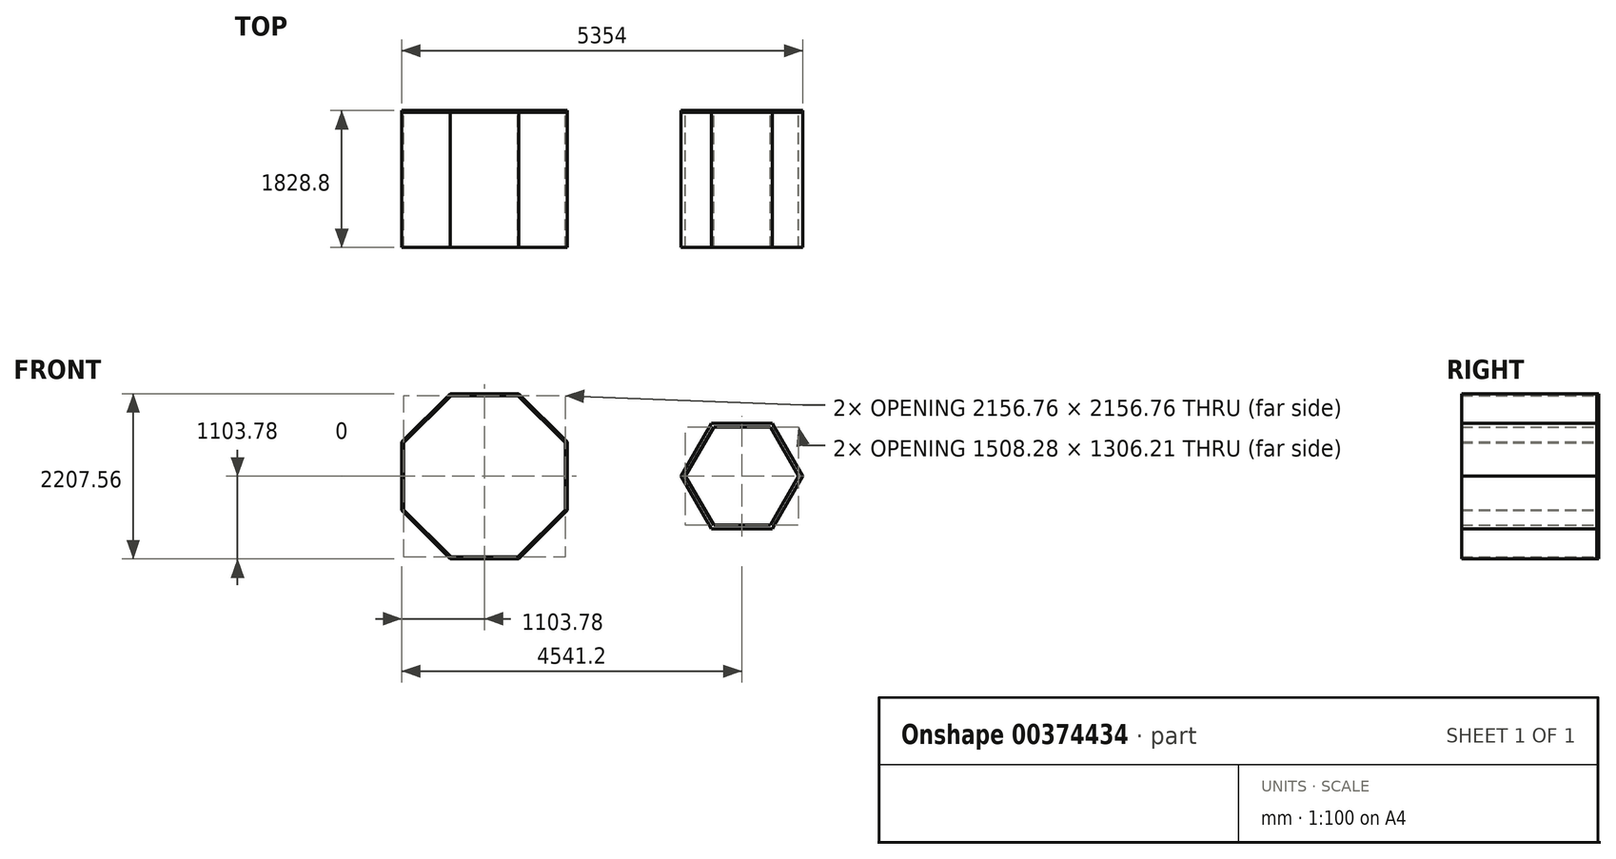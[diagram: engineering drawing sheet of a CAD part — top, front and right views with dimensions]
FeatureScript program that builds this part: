
annotation { "Feature Type Name" : "Feature", "Feature Type Description" : "" }
export const myFeature = defineFeature(function(context is Context, id is Id, definition is map)
    precondition{}
    {
        {
            var Q0;
            Q0=qCreatedBy(makeId("Front.planeOp"),FACE);
            var sketch = newSketch(context, id + "F0", { "sketchPlane" : qUnion([Q0])});
            skCircle(sketch, "E0.cCircle", {"center": v(0, 0) * mm, "radius": 812.8 * mm, "construction": true});
            skLineSegment(sketch, "E0.0", {"start": v(812.8, 0) * mm, "end": v(406.4, -703.9) * mm});
            skLineSegment(sketch, "E0.1", {"start": v(406.4, -703.9) * mm, "end": v(-406.4, -703.9) * mm});
            skLineSegment(sketch, "E0.2", {"start": v(-406.4, -703.9) * mm, "end": v(-812.8, 0) * mm});
            skLineSegment(sketch, "E0.3", {"start": v(-812.8, 0) * mm, "end": v(-406.4, 703.9) * mm});
            skLineSegment(sketch, "E0.4", {"start": v(-406.4, 703.9) * mm, "end": v(406.4, 703.9) * mm});
            skLineSegment(sketch, "E0.5", {"start": v(406.4, 703.9) * mm, "end": v(812.8, 0) * mm});
            skLineSegment(sketch, "E1.0", {"start": v(-754.14, 0) * mm, "end": v(-377.07, 653.1) * mm});
            skLineSegment(sketch, "E1.1", {"start": v(377.07, 653.1) * mm, "end": v(754.14, 0) * mm});
            skLineSegment(sketch, "E1.2", {"start": v(754.14, 0) * mm, "end": v(377.07, -653.1) * mm});
            skLineSegment(sketch, "E1.3", {"start": v(-377.07, 653.1) * mm, "end": v(377.07, 653.1) * mm});
            skLineSegment(sketch, "E1.4", {"start": v(377.07, -653.1) * mm, "end": v(-377.07, -653.1) * mm});
            skLineSegment(sketch, "E1.5", {"start": v(-377.07, -653.1) * mm, "end": v(-754.14, 0) * mm});
            skCircle(sketch, "E2.cCircle", {"center": v(-3437.42, 0) * mm, "radius": 1103.78 * mm, "construction": true});
            skLineSegment(sketch, "E2.0", {"start": v(-2980.22, -1103.78) * mm, "end": v(-3894.62, -1103.78) * mm});
            skLineSegment(sketch, "E2.1", {"start": v(-3894.62, -1103.78) * mm, "end": v(-4541.2, -457.2) * mm});
            skLineSegment(sketch, "E2.2", {"start": v(-4541.2, -457.2) * mm, "end": v(-4541.2, 457.2) * mm});
            skLineSegment(sketch, "E2.3", {"start": v(-4541.2, 457.2) * mm, "end": v(-3894.62, 1103.78) * mm});
            skLineSegment(sketch, "E2.4", {"start": v(-3894.62, 1103.78) * mm, "end": v(-2980.22, 1103.78) * mm});
            skLineSegment(sketch, "E2.5", {"start": v(-2980.22, 1103.78) * mm, "end": v(-2333.64, 457.2) * mm});
            skLineSegment(sketch, "E2.6", {"start": v(-2333.64, 457.2) * mm, "end": v(-2333.64, -457.2) * mm});
            skLineSegment(sketch, "E2.7", {"start": v(-2333.64, -457.2) * mm, "end": v(-2980.22, -1103.78) * mm});
            skPoint(sketch, "E2.0.midPoint", {"position": v(-3437.42, -1103.78) * mm});
            skLineSegment(sketch, "E3.0", {"start": v(-4515.8, 446.68) * mm, "end": v(-3884.1, 1078.38) * mm});
            skLineSegment(sketch, "E3.1", {"start": v(-4515.8, -446.68) * mm, "end": v(-4515.8, 446.68) * mm});
            skLineSegment(sketch, "E3.2", {"start": v(-3884.1, 1078.38) * mm, "end": v(-2990.74, 1078.38) * mm});
            skLineSegment(sketch, "E3.3", {"start": v(-3884.1, -1078.38) * mm, "end": v(-4515.8, -446.68) * mm});
            skLineSegment(sketch, "E3.4", {"start": v(-2990.74, 1078.38) * mm, "end": v(-2359.04, 446.68) * mm});
            skLineSegment(sketch, "E3.5", {"start": v(-2359.04, 446.68) * mm, "end": v(-2359.04, -446.68) * mm});
            skLineSegment(sketch, "E3.6", {"start": v(-2359.04, -446.68) * mm, "end": v(-2990.74, -1078.38) * mm});
            skLineSegment(sketch, "E3.7", {"start": v(-2990.74, -1078.38) * mm, "end": v(-3884.1, -1078.38) * mm});
            skSolve(sketch);
        }
        {
            var Q0;
            Q0 = qSketchRegion(id + "F0", true);
            extrude(context, id + "F1", {"entities" : qUnion([Q0]), "depth" : 1828.8 * mm});
        }
        {
            var Q0;
            Q0 = qSketchRegion(id + "F0", true);
            extrude(context, id + "F2", {"entities" : qUnion([Q0]), "depth" : 25.4 * mm});
        }
    });
